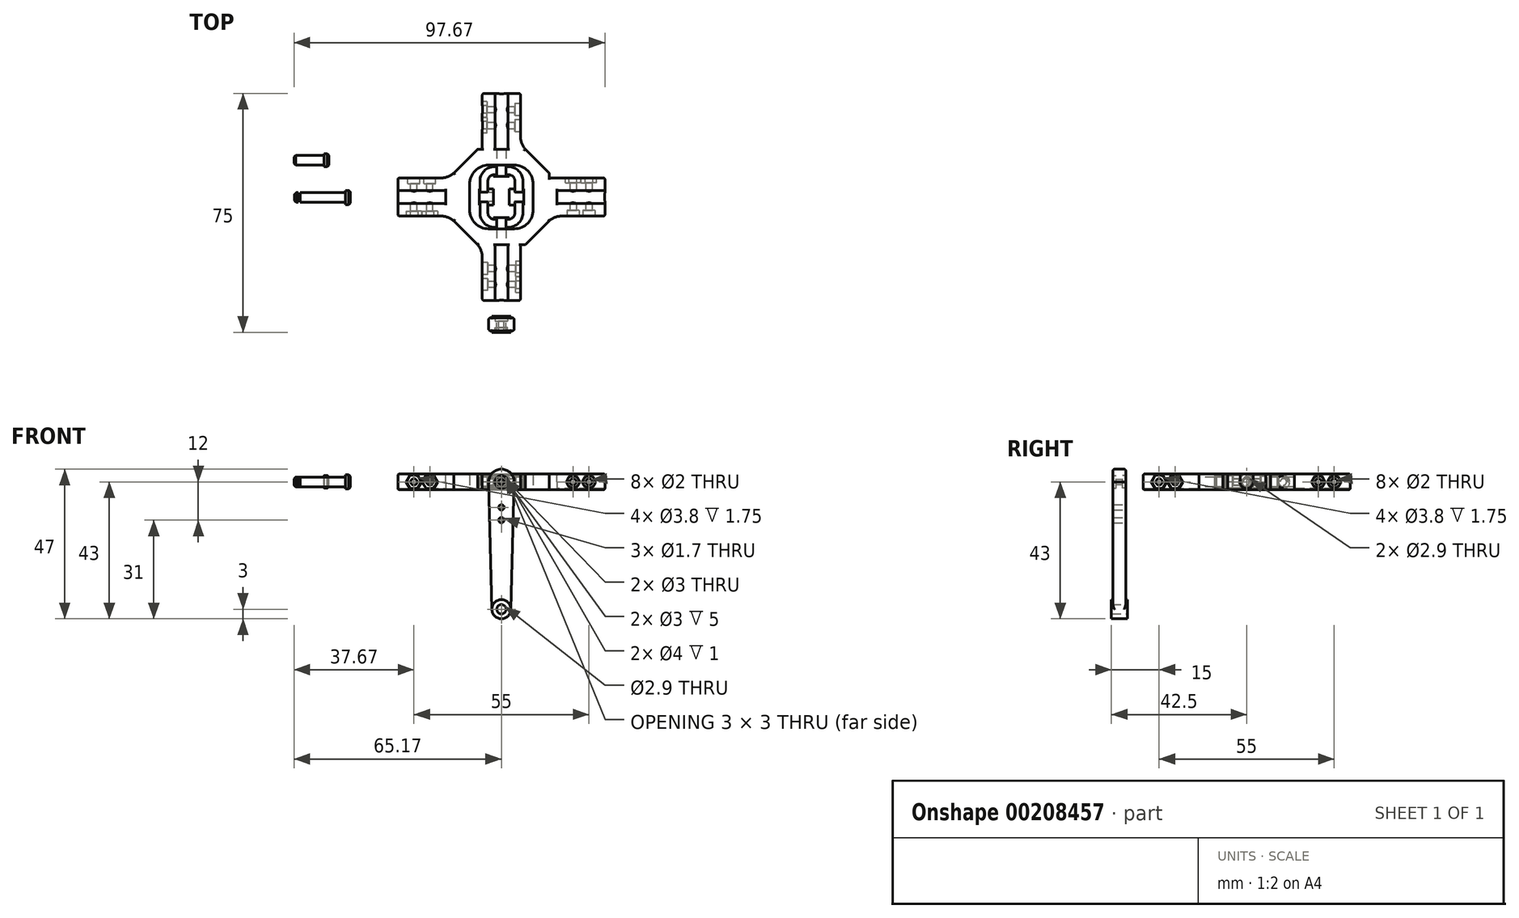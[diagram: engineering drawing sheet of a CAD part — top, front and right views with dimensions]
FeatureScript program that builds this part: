
annotation { "Feature Type Name" : "Feature", "Feature Type Description" : "" }
export const myFeature = defineFeature(function(context is Context, id is Id, definition is map)
    precondition{}
    {
        {
            var Q0;
            Q0=qCreatedBy(makeId("Front.planeOp"),FACE);
            var sketch = newSketch(context, id + "F0", { "sketchPlane" : qUnion([Q0])});
            skCircle(sketch, "E0", {"center": v(0, 0) * mm, "radius": 4 * mm});
            skCircle(sketch, "E1", {"center": v(0, -40) * mm, "radius": 3 * mm});
            skCircle(sketch, "E2", {"center": v(0, -40) * mm, "radius": 1.45 * mm});
            skLineSegment(sketch, "E3", {"start": v(-2, -37.76) * mm, "end": v(-2, -3.46) * mm});
            skLineSegment(sketch, "E4.MirrorCS", {"start": v(2, -37.76) * mm, "end": v(2, -3.46) * mm});
            skCircle(sketch, "E5", {"center": v(0, 0) * mm, "radius": 0.85 * mm});
            skCircle(sketch, "E6", {"center": v(0, -8) * mm, "radius": 0.85 * mm});
            skCircle(sketch, "E7", {"center": v(0, -12) * mm, "radius": 0.85 * mm});
            skCircle(sketch, "E8", {"center": v(0, 0) * mm, "radius": 2 * mm});
            skLineSegment(sketch, "E9", {"start": v(-4, 0) * mm, "end": v(-3, -40.07) * mm});
            skLineSegment(sketch, "E10", {"start": v(4, 0) * mm, "end": v(3, -40.07) * mm});
            skSolve(sketch);
        }
        {
            var Q0;
            {var subQ0=sQuery(id+"F0.wireOp",EDGE,"E0");var subQ1=makeQuery(id+"F0.imprint","INTERSECT",VERTEX,{"derivedFrom":[subQ0,sQuery(id+"F0.wireOp",EDGE,"E3")]});Q0=makeQuery(id+"F0.imprint","IMPRINT",FACE,{"disambiguationData":[TD([[makeQuery(id+"F0.imprint","IMPRINT",EDGE,{"disambiguationData":[TD([[subQ1,-1.0]])],"derivedFrom":subQ0}),1.0]])]});}
            var Q1;
            {var subQ0=sQuery(id+"F0.wireOp",EDGE,"E3");Q1=makeQuery(id+"F0.imprint","IMPRINT",FACE,{"disambiguationData":[TD([[makeQuery(id+"F0.imprint","IMPRINT",EDGE,{"derivedFrom":subQ0}),-1.0]])]});}
            var Q2;
            Q2=makeQuery(id+"F0.imprint","IMPRINT",FACE,{"disambiguationData":[TD([[makeQuery(id+"F0.imprint","IMPRINT",EDGE,{"derivedFrom":sQuery(id+"F0.wireOp",EDGE,"E5")}),-1.0]])]});
            var Q3;
            {var subQ0=sQuery(id+"F0.wireOp",EDGE,"E3");Q3=makeQuery(id+"F0.imprint","IMPRINT",FACE,{"disambiguationData":[TD([[makeQuery(id+"F0.imprint","IMPRINT",EDGE,{"derivedFrom":subQ0}),1.0]])]});}
            var Q4;
            {var subQ0=sQuery(id+"F0.wireOp",EDGE,"E4.MirrorCS");Q4=makeQuery(id+"F0.imprint","IMPRINT",FACE,{"disambiguationData":[TD([[makeQuery(id+"F0.imprint","IMPRINT",EDGE,{"derivedFrom":subQ0}),-1.0]])]});}
            extrude(context, id + "F1", {"entities" : qUnion([Q0, Q1, Q2, Q3, Q4]), "endBound" : BoundingType.SYMMETRIC, "depth" : 4 * mm});
        }
        {
            var Q0;
            Q0=makeQuery(id+"F0.imprint","IMPRINT",FACE,{"disambiguationData":[TD([[makeQuery(id+"F0.imprint","IMPRINT",EDGE,{"derivedFrom":sQuery(id+"F0.wireOp",EDGE,"E2")}),-1.0]])]});
            extrude(context, id + "F2", {"entities" : qUnion([Q0]), "operationType" : NewBodyOperationType.ADD, "endBound" : BoundingType.SYMMETRIC, "depth" : 5 * mm});
        }
        {
            var Q0;
            Q0=makeQuery(id+"F1.opExtrude","CAP_EDGE",EDGE,{"disambiguationData":[OSD([sQuery(id+"F0.wireOp",EDGE,"E9")])],"isStart":false});
            var Q1;
            Q1=makeQuery(id+"F1.opExtrude","CAP_EDGE",EDGE,{"disambiguationData":[OSD([sQuery(id+"F0.wireOp",EDGE,"E9")])],"isStart":true});
            var Q2;
            Q2=makeQuery(id+"F1.opExtrude","CAP_EDGE",EDGE,{"disambiguationData":[OSD([sQuery(id+"F0.wireOp",EDGE,"E10")])],"isStart":false});
            var Q3;
            Q3=makeQuery(id+"F1.opExtrude","CAP_EDGE",EDGE,{"disambiguationData":[OSD([sQuery(id+"F0.wireOp",EDGE,"E10")])],"isStart":true});
            var Q4;
            Q4=makeQuery(id+"F1.opExtrude","CAP_EDGE",EDGE,{"disambiguationData":[OSD([sQuery(id+"F0.wireOp",EDGE,"E0")])],"isStart":false});
            var Q5;
            Q5=makeQuery(id+"F1.opExtrude","CAP_EDGE",EDGE,{"disambiguationData":[OSD([sQuery(id+"F0.wireOp",EDGE,"E0")])],"isStart":true});
            fillet(context, id + "F3", {"entities" : qUnion([Q0, Q1, Q2, Q3, Q4, Q5]), "radius" : 0.5 * mm, "allowEdgeOverflow" : false});
        }
        {
            var Q0;
            Q0=makeQuery(id+"F0.imprint","IMPRINT",FACE,{"disambiguationData":[TD([[makeQuery(id+"F0.imprint","IMPRINT",EDGE,{"derivedFrom":sQuery(id+"F0.wireOp",EDGE,"E5")}),-1.0]])]});
            extrude(context, id + "F4", {"entities" : qUnion([Q0]), "operationType" : NewBodyOperationType.REMOVE, "depth" : 2 * mm, "hasSecondDirection" : true, "secondDirectionOppositeDirection" : false, "secondDirectionDepth" : 1 * mm});
        }
        {
            var Q0;
            Q0=makeQuery(id+"F0.imprint","IMPRINT",FACE,{"disambiguationData":[TD([[makeQuery(id+"F0.imprint","IMPRINT",EDGE,{"derivedFrom":sQuery(id+"F0.wireOp",EDGE,"E5")}),-1.0]])]});
            extrude(context, id + "F5", {"entities" : qUnion([Q0]), "operationType" : NewBodyOperationType.REMOVE, "oppositeDirection" : true, "depth" : 2 * mm, "hasSecondDirection" : true, "secondDirectionOppositeDirection" : true, "secondDirectionDepth" : 1 * mm});
        }
        {
            var Q0;
            Q0=qCreatedBy(makeId("Top.planeOp"),FACE);
            var sketch = newSketch(context, id + "F6", { "sketchPlane" : qUnion([Q0])});
            skLineSegment(sketch, "E11", {"start": v(7, 40) * mm, "end": v(-7, 40) * mm});
            skLineSegment(sketch, "E12", {"start": v(7, 40) * mm, "end": v(7, 42.5) * mm});
            skLineSegment(sketch, "E13", {"start": v(7, 42.5) * mm, "end": v(2.5, 42.5) * mm});
            skLineSegment(sketch, "E14", {"start": v(2.5, 42.5) * mm, "end": v(2.5, 40) * mm});
            skLineSegment(sketch, "E15.MirrorCS", {"start": v(-7, 40) * mm, "end": v(-7, 42.5) * mm});
            skLineSegment(sketch, "E16.MirrorCS", {"start": v(-7, 42.5) * mm, "end": v(-2.5, 42.5) * mm});
            skLineSegment(sketch, "E17.MirrorCS", {"start": v(-2.5, 42.5) * mm, "end": v(-2.5, 40) * mm});
            skLineSegment(sketch, "E18", {"start": v(0, 30) * mm, "end": v(0, 50) * mm});
            skLineSegment(sketch, "E19", {"start": v(0, 33.5) * mm, "end": v(-2.5, 33.5) * mm});
            skLineSegment(sketch, "E20", {"start": v(-2.5, 33.5) * mm, "end": v(-2.5, 30) * mm});
            skLineSegment(sketch, "E21.MirrorCS", {"start": v(0, 46.5) * mm, "end": v(-2.5, 46.5) * mm});
            skLineSegment(sketch, "E22.MirrorCS", {"start": v(-2.5, 46.5) * mm, "end": v(-2.5, 50) * mm});
            skLineSegment(sketch, "E23.bottom", {"start": v(-2.25, 49.5) * mm, "end": v(2.25, 49.5) * mm});
            skLineSegment(sketch, "E23.top", {"start": v(-2.25, 30.5) * mm, "end": v(2.25, 30.5) * mm});
            skLineSegment(sketch, "E23.left", {"start": v(-6.75, 45) * mm, "end": v(-6.75, 35) * mm});
            skLineSegment(sketch, "E23.right", {"start": v(6.75, 45) * mm, "end": v(6.75, 35) * mm});
            skLineSegment(sketch, "E24.bottom", {"start": v(-2.25, 47) * mm, "end": v(2.25, 47) * mm});
            skLineSegment(sketch, "E24.top", {"start": v(-2.25, 33) * mm, "end": v(2.25, 33) * mm});
            skLineSegment(sketch, "E24.left", {"start": v(-4.25, 45) * mm, "end": v(-4.25, 35) * mm});
            skLineSegment(sketch, "E24.right", {"start": v(4.25, 45) * mm, "end": v(4.25, 35) * mm});
            skLineSegment(sketch, "E25", {"start": v(-2.5, 30) * mm, "end": v(0, 30) * mm});
            skLineSegment(sketch, "E26.MirrorCS", {"start": v(-2.5, 50) * mm, "end": v(0, 50) * mm});
            skPoint(sketch, "E27.visualSharp", {"position": v(-4.25, 47) * mm});
            skArc(sketch, "E27.filletArc", {"start": v(-2.25, 47) * mm, "mid": v(-3.66, 46.41) * mm, "end": v(-4.25, 45) * mm});
            skPoint(sketch, "E28.visualSharp", {"position": v(4.25, 47) * mm});
            skArc(sketch, "E28.filletArc", {"start": v(4.25, 45) * mm, "mid": v(3.66, 46.41) * mm, "end": v(2.25, 47) * mm});
            skPoint(sketch, "E29.visualSharp", {"position": v(4.25, 33) * mm});
            skArc(sketch, "E29.filletArc", {"start": v(2.25, 33) * mm, "mid": v(3.66, 33.59) * mm, "end": v(4.25, 35) * mm});
            skPoint(sketch, "E30.visualSharp", {"position": v(-4.25, 33) * mm});
            skArc(sketch, "E30.filletArc", {"start": v(-4.25, 35) * mm, "mid": v(-3.66, 33.59) * mm, "end": v(-2.25, 33) * mm});
            skPoint(sketch, "E31.visualSharp", {"position": v(-6.75, 49.5) * mm});
            skArc(sketch, "E31.filletArc", {"start": v(-2.25, 49.5) * mm, "mid": v(-5.43, 48.18) * mm, "end": v(-6.75, 45) * mm});
            skPoint(sketch, "E32.visualSharp", {"position": v(6.75, 49.5) * mm});
            skArc(sketch, "E32.filletArc", {"start": v(6.75, 45) * mm, "mid": v(5.43, 48.18) * mm, "end": v(2.25, 49.5) * mm});
            skPoint(sketch, "E33.visualSharp", {"position": v(-6.75, 30.5) * mm});
            skArc(sketch, "E33.filletArc", {"start": v(-6.75, 35) * mm, "mid": v(-5.43, 31.82) * mm, "end": v(-2.25, 30.5) * mm});
            skPoint(sketch, "E34.visualSharp", {"position": v(6.75, 30.5) * mm});
            skArc(sketch, "E34.filletArc", {"start": v(2.25, 30.5) * mm, "mid": v(5.43, 31.82) * mm, "end": v(6.75, 35) * mm});
            skSolve(sketch);
        }
        {
            var Q0;
            {var subQ1=sQuery(id+"F6.wireOp",EDGE,"E23.left");var subQ3=sQuery(id+"F6.wireOp",EDGE,"E16.MirrorCS");var subQ4=makeQuery(id+"F6.imprint","INTERSECT",VERTEX,{"derivedFrom":[subQ3,subQ1]});Q0=makeQuery(id+"F6.imprint","IMPRINT",FACE,{"disambiguationData":[TD([[makeQuery(id+"F6.imprint","IMPRINT",EDGE,{"disambiguationData":[TD([[subQ4,-1.0]])],"derivedFrom":subQ3}),1.0]])]});}
            var Q1;
            {var subQ3=sQuery(id+"F6.wireOp",EDGE,"E18");var subQ8=sQuery(id+"F6.wireOp",EDGE,"E23.bottom");var subQ10=makeQuery(id+"F6.imprint","INTERSECT",VERTEX,{"derivedFrom":[subQ3,subQ8]});Q1=makeQuery(id+"F6.imprint","IMPRINT",FACE,{"disambiguationData":[TD([[makeQuery(id+"F6.imprint","IMPRINT",EDGE,{"disambiguationData":[TD([[subQ10,1.0]])],"derivedFrom":subQ3}),1.0]])]});}
            var Q2;
            {var subQ9=sQuery(id+"F6.wireOp",EDGE,"E28.filletArc");Q2=makeQuery(id+"F6.imprint","IMPRINT",FACE,{"disambiguationData":[TD([[makeQuery(id+"F6.imprint","IMPRINT",EDGE,{"derivedFrom":subQ9}),-1.0]])]});}
            var Q3;
            {var subQ0=sQuery(id+"F6.wireOp",EDGE,"E23.right");var subQ1=sQuery(id+"F6.wireOp",EDGE,"E11");var subQ2=makeQuery(id+"F6.imprint","INTERSECT",VERTEX,{"derivedFrom":[subQ1,subQ0]});Q3=makeQuery(id+"F6.imprint","IMPRINT",FACE,{"disambiguationData":[TD([[makeQuery(id+"F6.imprint","IMPRINT",EDGE,{"disambiguationData":[TD([[subQ2,-1.0]])],"derivedFrom":subQ1}),-1.0]])]});}
            var Q4;
            {var subQ7=sQuery(id+"F6.wireOp",EDGE,"E29.filletArc");Q4=makeQuery(id+"F6.imprint","IMPRINT",FACE,{"disambiguationData":[TD([[makeQuery(id+"F6.imprint","IMPRINT",EDGE,{"derivedFrom":subQ7}),-1.0]])]});}
            var Q5;
            {var subQ1=sQuery(id+"F6.wireOp",EDGE,"E23.top");var subQ3=sQuery(id+"F6.wireOp",EDGE,"E18");var subQ4=makeQuery(id+"F6.imprint","INTERSECT",VERTEX,{"derivedFrom":[subQ3,subQ1]});Q5=makeQuery(id+"F6.imprint","IMPRINT",FACE,{"disambiguationData":[TD([[makeQuery(id+"F6.imprint","IMPRINT",EDGE,{"disambiguationData":[TD([[subQ4,-1.0]])],"derivedFrom":subQ3}),1.0]])]});}
            var Q6;
            {var subQ1=sQuery(id+"F6.wireOp",EDGE,"E23.left");var subQ3=sQuery(id+"F6.wireOp",EDGE,"E11");var subQ4=makeQuery(id+"F6.imprint","INTERSECT",VERTEX,{"derivedFrom":[subQ3,subQ1]});Q6=makeQuery(id+"F6.imprint","IMPRINT",FACE,{"disambiguationData":[TD([[makeQuery(id+"F6.imprint","IMPRINT",EDGE,{"disambiguationData":[TD([[subQ4,1.0]])],"derivedFrom":subQ3}),1.0]])]});}
            var Q7;
            {var subQ0=sQuery(id+"F6.wireOp",EDGE,"E23.left");var subQ1=sQuery(id+"F6.wireOp",EDGE,"E11");var subQ2=makeQuery(id+"F6.imprint","INTERSECT",VERTEX,{"derivedFrom":[subQ1,subQ0]});Q7=makeQuery(id+"F6.imprint","IMPRINT",FACE,{"disambiguationData":[TD([[makeQuery(id+"F6.imprint","IMPRINT",EDGE,{"disambiguationData":[TD([[subQ2,1.0]])],"derivedFrom":subQ1}),-1.0]])]});}
            extrude(context, id + "F7", {"entities" : qUnion([Q0, Q1, Q2, Q3, Q4, Q5, Q6, Q7]), "endBound" : BoundingType.SYMMETRIC, "depth" : 4 * mm});
        }
        {
            var Q0;
            {var subQ0=sQuery(id+"F6.wireOp",EDGE,"E17.MirrorCS");Q0=makeQuery(id+"F6.imprint","IMPRINT",FACE,{"disambiguationData":[TD([[makeQuery(id+"F6.imprint","IMPRINT",EDGE,{"derivedFrom":subQ0}),-1.0]])]});}
            var Q1;
            {var subQ0=sQuery(id+"F6.wireOp",EDGE,"E15.MirrorCS");Q1=makeQuery(id+"F6.imprint","IMPRINT",FACE,{"disambiguationData":[TD([[makeQuery(id+"F6.imprint","IMPRINT",EDGE,{"derivedFrom":subQ0}),-1.0]])]});}
            var Q2;
            {var subQ0=sQuery(id+"F6.wireOp",EDGE,"E23.left");var subQ1=sQuery(id+"F6.wireOp",EDGE,"E11");var subQ2=makeQuery(id+"F6.imprint","INTERSECT",VERTEX,{"derivedFrom":[subQ1,subQ0]});Q2=makeQuery(id+"F6.imprint","IMPRINT",FACE,{"disambiguationData":[TD([[makeQuery(id+"F6.imprint","IMPRINT",EDGE,{"disambiguationData":[TD([[subQ2,1.0]])],"derivedFrom":subQ1}),-1.0]])]});}
            var Q3;
            {var subQ0=sQuery(id+"F6.wireOp",EDGE,"E14");Q3=makeQuery(id+"F6.imprint","IMPRINT",FACE,{"disambiguationData":[TD([[makeQuery(id+"F6.imprint","IMPRINT",EDGE,{"derivedFrom":subQ0}),1.0]])]});}
            var Q4;
            {var subQ0=sQuery(id+"F6.wireOp",EDGE,"E23.right");var subQ1=sQuery(id+"F6.wireOp",EDGE,"E11");var subQ2=makeQuery(id+"F6.imprint","INTERSECT",VERTEX,{"derivedFrom":[subQ1,subQ0]});Q4=makeQuery(id+"F6.imprint","IMPRINT",FACE,{"disambiguationData":[TD([[makeQuery(id+"F6.imprint","IMPRINT",EDGE,{"disambiguationData":[TD([[subQ2,-1.0]])],"derivedFrom":subQ1}),-1.0]])]});}
            var Q5;
            {var subQ0=sQuery(id+"F6.wireOp",EDGE,"E12");Q5=makeQuery(id+"F6.imprint","IMPRINT",FACE,{"disambiguationData":[TD([[makeQuery(id+"F6.imprint","IMPRINT",EDGE,{"derivedFrom":subQ0}),1.0]])]});}
            var Q6;
            Q6=sQuery(id+"F6.wireOp",EDGE,"E11");
            revolve(context, id + "F8", {"operationType" : NewBodyOperationType.ADD, "entities" : qUnion([Q0, Q1, Q2, Q3, Q4, Q5]), "axis" : qUnion([Q6]), "revolveType" : RevolveType.FULL});
        }
        {
            var Q0;
            {var subQ0=sQuery(id+"F6.wireOp",EDGE,"LlKhZmQs-V7VM-scmc-Wy5A-JgZZQCK02wPD");Q0=makeQuery(id+"F6.imprint","IMPRINT",FACE,{"disambiguationData":[TD([[makeQuery(id+"F6.imprint","IMPRINT",EDGE,{"derivedFrom":subQ0}),1.0]])]});}
            var Q1;
            {var subQ1=sQuery(id+"F6.wireOp",EDGE,"n0KZ0Nd7-8ER9-4vQ4-z3Lu-z5KG9LSxnQ1L");var subQ3=sQuery(id+"F6.wireOp",EDGE,"E20");var subQ4=makeQuery(id+"F6.imprint","INTERSECT",VERTEX,{"derivedFrom":[subQ1,subQ3]});Q1=makeQuery(id+"F6.imprint","IMPRINT",FACE,{"disambiguationData":[TD([[makeQuery(id+"F6.imprint","IMPRINT",EDGE,{"disambiguationData":[TD([[subQ4,-1.0]])],"derivedFrom":subQ1}),1.0]])]});}
            var Q2;
            {var subQ0=sQuery(id+"F6.wireOp",EDGE,"E19");Q2=makeQuery(id+"F6.imprint","IMPRINT",FACE,{"disambiguationData":[TD([[makeQuery(id+"F6.imprint","IMPRINT",EDGE,{"derivedFrom":subQ0}),1.0]])]});}
            var Q3;
            {var subQ0=sQuery(id+"F6.wireOp",EDGE,"E21.MirrorCS");Q3=makeQuery(id+"F6.imprint","IMPRINT",FACE,{"disambiguationData":[TD([[makeQuery(id+"F6.imprint","IMPRINT",EDGE,{"derivedFrom":subQ0}),-1.0]])]});}
            var Q4;
            {var subQ1=sQuery(id+"F6.wireOp",EDGE,"n0KZ0Nd7-8ER9-4vQ4-z3Lu-z5KG9LSxnQ1L");var subQ3=sQuery(id+"F6.wireOp",EDGE,"E22.MirrorCS");var subQ4=makeQuery(id+"F6.imprint","INTERSECT",VERTEX,{"derivedFrom":[subQ1,subQ3]});Q4=makeQuery(id+"F6.imprint","IMPRINT",FACE,{"disambiguationData":[TD([[makeQuery(id+"F6.imprint","IMPRINT",EDGE,{"disambiguationData":[TD([[subQ4,1.0]])],"derivedFrom":subQ1}),1.0]])]});}
            var Q5;
            {var subQ0=sQuery(id+"F6.wireOp",EDGE,"13f33fd6-691d-4f27-a9ab-e85cbf9f38f40.MirrorCS");Q5=makeQuery(id+"F6.imprint","IMPRINT",FACE,{"disambiguationData":[TD([[makeQuery(id+"F6.imprint","IMPRINT",EDGE,{"derivedFrom":subQ0}),-1.0]])]});}
            var Q6;
            {var subQ3=sQuery(id+"F6.wireOp",EDGE,"E18");var subQ8=sQuery(id+"F6.wireOp",EDGE,"E23.bottom");var subQ10=makeQuery(id+"F6.imprint","INTERSECT",VERTEX,{"derivedFrom":[subQ3,subQ8]});Q6=makeQuery(id+"F6.imprint","IMPRINT",FACE,{"disambiguationData":[TD([[makeQuery(id+"F6.imprint","IMPRINT",EDGE,{"disambiguationData":[TD([[subQ10,1.0]])],"derivedFrom":subQ3}),1.0]])]});}
            var Q7;
            {var subQ0=sQuery(id+"F6.wireOp",EDGE,"E26.MirrorCS");Q7=makeQuery(id+"F6.imprint","IMPRINT",FACE,{"disambiguationData":[TD([[makeQuery(id+"F6.imprint","IMPRINT",EDGE,{"derivedFrom":subQ0}),-1.0]])]});}
            var Q8;
            {var subQ1=sQuery(id+"F6.wireOp",EDGE,"E23.top");var subQ3=sQuery(id+"F6.wireOp",EDGE,"E18");var subQ4=makeQuery(id+"F6.imprint","INTERSECT",VERTEX,{"derivedFrom":[subQ3,subQ1]});Q8=makeQuery(id+"F6.imprint","IMPRINT",FACE,{"disambiguationData":[TD([[makeQuery(id+"F6.imprint","IMPRINT",EDGE,{"disambiguationData":[TD([[subQ4,-1.0]])],"derivedFrom":subQ3}),1.0]])]});}
            var Q9;
            {var subQ0=sQuery(id+"F6.wireOp",EDGE,"E25");Q9=makeQuery(id+"F6.imprint","IMPRINT",FACE,{"disambiguationData":[TD([[makeQuery(id+"F6.imprint","IMPRINT",EDGE,{"derivedFrom":subQ0}),1.0]])]});}
            var Q10;
            Q10=sQuery(id+"F6.wireOp",EDGE,"E18");
            revolve(context, id + "F9", {"operationType" : NewBodyOperationType.ADD, "entities" : qUnion([Q0, Q1, Q2, Q3, Q4, Q5, Q6, Q7, Q8, Q9]), "axis" : qUnion([Q10]), "revolveType" : RevolveType.FULL});
        }
        {
            var Q0;
            Q0=makeQuery(id+"F8.opRevolve","SWEPT_FACE",FACE,{"disambiguationData":[OSD([sQuery(id+"F6.wireOp",EDGE,"E15.MirrorCS")])]});
            var sketch = newSketch(context, id + "F10", { "sketchPlane" : qUnion([Q0])});
            skCircle(sketch, "E35", {"center": v(-40, 0) * mm, "radius": 1.45 * mm});
            skSolve(sketch);
        }
        {
            var Q0;
            Q0=makeQuery(id+"F10.imprint","IMPRINT",FACE,{"disambiguationData":[TD([[makeQuery(id+"F10.imprint","IMPRINT",EDGE,{"derivedFrom":sQuery(id+"F10.wireOp",EDGE,"E35")}),1.0]])]});
            extrude(context, id + "F11", {"entities" : qUnion([Q0]), "operationType" : NewBodyOperationType.REMOVE, "endBound" : BoundingType.THROUGH_ALL, "oppositeDirection" : true, "depth" : 25 * mm});
        }
        {
            var Q0;
            Q0=makeQuery(id+"F9.opRevolve","SWEPT_FACE",FACE,{"disambiguationData":[OSD([sQuery(id+"F6.wireOp",EDGE,"E25")])]});
            var sketch = newSketch(context, id + "F12", { "sketchPlane" : qUnion([Q0])});
            skCircle(sketch, "E36", {"center": v(0, 0) * mm, "radius": 1.5 * mm});
            skSolve(sketch);
        }
        {
            var Q0;
            Q0=makeQuery(id+"F12.imprint","IMPRINT",FACE,{"disambiguationData":[TD([[makeQuery(id+"F12.imprint","IMPRINT",EDGE,{"derivedFrom":sQuery(id+"F12.wireOp",EDGE,"E36")}),1.0]])]});
            extrude(context, id + "F13", {"entities" : qUnion([Q0]), "operationType" : NewBodyOperationType.REMOVE, "endBound" : BoundingType.THROUGH_ALL, "oppositeDirection" : true, "depth" : 25 * mm});
        }
        {
            var Q0;
            Q0=qCreatedBy(makeId("Top.planeOp"),FACE);
            var sketch = newSketch(context, id + "F14", { "sketchPlane" : qUnion([Q0])});
            skLineSegment(sketch, "E37.bottom", {"start": v(-10, 50) * mm, "end": v(10, 50) * mm});
            skLineSegment(sketch, "E37.top", {"start": v(-10, 30) * mm, "end": v(10, 30) * mm});
            skLineSegment(sketch, "E37.left", {"start": v(-10, 50) * mm, "end": v(-10, 30) * mm});
            skLineSegment(sketch, "E37.right", {"start": v(10, 50) * mm, "end": v(10, 30) * mm});
            skPoint(sketch, "E37.middle", {"position": v(0, 40) * mm});
            skCircle(sketch, "E38", {"center": v(0, 40) * mm, "radius": 10 * mm, "construction": true});
            skLineSegment(sketch, "E39.bottom", {"start": v(30, 10) * mm, "end": v(-30, 10) * mm});
            skLineSegment(sketch, "E39.top", {"start": v(30, 70) * mm, "end": v(-30, 70) * mm});
            skLineSegment(sketch, "E39.left", {"start": v(30, 10) * mm, "end": v(30, 70) * mm});
            skLineSegment(sketch, "E39.right", {"start": v(-30, 10) * mm, "end": v(-30, 70) * mm});
            skLineSegment(sketch, "E40", {"start": v(-7.5, 70) * mm, "end": v(-7.5, 55) * mm});
            skLineSegment(sketch, "E41", {"start": v(-7.5, 55) * mm, "end": v(-15, 47.5) * mm});
            skLineSegment(sketch, "E42", {"start": v(-15, 47.5) * mm, "end": v(-30, 47.5) * mm});
            skLineSegment(sketch, "E43", {"start": v(30, 70) * mm, "end": v(-30, 10) * mm, "construction": true});
            skLineSegment(sketch, "E44", {"start": v(-30, 40) * mm, "end": v(30, 40) * mm, "construction": true});
            skLineSegment(sketch, "E45.MirrorCS", {"start": v(30, 32.5) * mm, "end": v(15, 32.5) * mm});
            skLineSegment(sketch, "E46.MirrorCS", {"start": v(7.5, 25) * mm, "end": v(7.5, 10) * mm});
            skLineSegment(sketch, "E47.MirrorCS", {"start": v(15, 32.5) * mm, "end": v(7.5, 25) * mm});
            skLineSegment(sketch, "E48.MirrorCS", {"start": v(30, 47.5) * mm, "end": v(15, 47.5) * mm});
            skLineSegment(sketch, "E49.MirrorCS", {"start": v(15, 47.5) * mm, "end": v(7.5, 55) * mm});
            skLineSegment(sketch, "E50.MirrorCS", {"start": v(7.5, 55) * mm, "end": v(7.5, 70) * mm});
            skLineSegment(sketch, "E51.MirrorCS", {"start": v(-7.5, 10) * mm, "end": v(-7.5, 25) * mm});
            skLineSegment(sketch, "E52.MirrorCS", {"start": v(-7.5, 25) * mm, "end": v(-15, 32.5) * mm});
            skLineSegment(sketch, "E53.MirrorCS", {"start": v(-15, 32.5) * mm, "end": v(-30, 32.5) * mm});
            skLineSegment(sketch, "E54", {"start": v(-30, 42.05) * mm, "end": v(-15, 42.05) * mm});
            skLineSegment(sketch, "E55", {"start": v(-15, 42.05) * mm, "end": v(-15, 37.95) * mm});
            skLineSegment(sketch, "E56", {"start": v(-15, 37.95) * mm, "end": v(-30, 37.95) * mm});
            skLineSegment(sketch, "E57.MirrorCS", {"start": v(-2.05, 25) * mm, "end": v(-2.05, 10) * mm});
            skLineSegment(sketch, "E58.MirrorCS", {"start": v(2.05, 10) * mm, "end": v(2.05, 25) * mm});
            skLineSegment(sketch, "E59.MirrorCS", {"start": v(2.05, 25) * mm, "end": v(-2.05, 25) * mm});
            skLineSegment(sketch, "E60.MirrorCS", {"start": v(2.05, 70) * mm, "end": v(2.05, 55) * mm});
            skLineSegment(sketch, "E61.MirrorCS", {"start": v(2.05, 55) * mm, "end": v(-2.05, 55) * mm});
            skLineSegment(sketch, "E62.MirrorCS", {"start": v(-2.05, 55) * mm, "end": v(-2.05, 70) * mm});
            skLineSegment(sketch, "E63.MirrorCS", {"start": v(30, 42.05) * mm, "end": v(15, 42.05) * mm});
            skLineSegment(sketch, "E64.MirrorCS", {"start": v(15, 37.95) * mm, "end": v(30, 37.95) * mm});
            skLineSegment(sketch, "E65.MirrorCS", {"start": v(15, 42.05) * mm, "end": v(15, 37.95) * mm});
            skLineSegment(sketch, "E66", {"start": v(-7, 38.55) * mm, "end": v(-2.5, 38.55) * mm, "construction": true});
            skLineSegment(sketch, "E67", {"start": v(-2.5, 41.45) * mm, "end": v(-7, 41.45) * mm, "construction": true});
            skLineSegment(sketch, "E68", {"start": v(-15, 47.5) * mm, "end": v(-15, 32.5) * mm});
            skLineSegment(sketch, "E69", {"start": v(-7.5, 55) * mm, "end": v(7.5, 55) * mm});
            skLineSegment(sketch, "E70", {"start": v(15, 47.5) * mm, "end": v(15, 32.5) * mm});
            skLineSegment(sketch, "E71", {"start": v(7.5, 25) * mm, "end": v(-7.5, 25) * mm});
            skSolve(sketch);
        }
        {
            var Q0;
            {var subQ0=sQuery(id+"F14.wireOp",EDGE,"WiRYdTlx-Ytys-IKBb-qOmJ-XlPzdqFq3X80");var subQ1=sQuery(id+"F14.wireOp",EDGE,"hd7CA16K-ODOx-UwDL-788j-aqSsYlvFxQFE");var subQ2=makeQuery(id+"F14.imprint","INTERSECT",VERTEX,{"disambiguationData":[OD(1.0)],"derivedFrom":[subQ1,subQ0]});Q0=makeQuery(id+"F14.imprint","IMPRINT",FACE,{"disambiguationData":[TD([[makeQuery(id+"F14.imprint","IMPRINT",EDGE,{"disambiguationData":[TD([[subQ2,-1.0]])],"derivedFrom":subQ1}),-1.0]])]});}
            var Q1;
            {var subQ0=sQuery(id+"F14.wireOp",EDGE,"rD6La231-fMC7-wIai-GG1w-WcltRfGgBhv8");var subQ1=sQuery(id+"F14.wireOp",EDGE,"hd7CA16K-ODOx-UwDL-788j-aqSsYlvFxQFE");var subQ2=makeQuery(id+"F14.imprint","INTERSECT",VERTEX,{"derivedFrom":[subQ1,subQ0]});Q1=makeQuery(id+"F14.imprint","IMPRINT",FACE,{"disambiguationData":[TD([[makeQuery(id+"F14.imprint","IMPRINT",EDGE,{"disambiguationData":[TD([[subQ2,-1.0]])],"derivedFrom":subQ1}),-1.0]])]});}
            var Q2;
            {var subQ0=sQuery(id+"F14.wireOp",EDGE,"WiRYdTlx-Ytys-IKBb-qOmJ-XlPzdqFq3X80");var subQ1=sQuery(id+"F14.wireOp",EDGE,"hd7CA16K-ODOx-UwDL-788j-aqSsYlvFxQFE");var subQ2=makeQuery(id+"F14.imprint","INTERSECT",VERTEX,{"disambiguationData":[OD(0.0)],"derivedFrom":[subQ1,subQ0]});Q2=makeQuery(id+"F14.imprint","IMPRINT",FACE,{"disambiguationData":[TD([[makeQuery(id+"F14.imprint","IMPRINT",EDGE,{"disambiguationData":[TD([[subQ2,1.0]])],"derivedFrom":subQ1}),-1.0]])]});}
            var Q3;
            {var subQ0=sQuery(id+"F14.wireOp",EDGE,"7f476OY6-gB4X-IM5u-cAVR-7MiV8QXeFFAP");var subQ1=sQuery(id+"F14.wireOp",EDGE,"hd7CA16K-ODOx-UwDL-788j-aqSsYlvFxQFE");var subQ2=makeQuery(id+"F14.imprint","INTERSECT",VERTEX,{"disambiguationData":[OD(0.0)],"derivedFrom":[subQ1,subQ0]});Q3=makeQuery(id+"F14.imprint","IMPRINT",FACE,{"disambiguationData":[TD([[makeQuery(id+"F14.imprint","IMPRINT",EDGE,{"disambiguationData":[TD([[subQ2,1.0]])],"derivedFrom":subQ1}),-1.0]])]});}
            var Q4;
            {var subQ0=sQuery(id+"F14.wireOp",EDGE,"7f476OY6-gB4X-IM5u-cAVR-7MiV8QXeFFAP");var subQ1=sQuery(id+"F14.wireOp",EDGE,"hd7CA16K-ODOx-UwDL-788j-aqSsYlvFxQFE");var subQ2=makeQuery(id+"F14.imprint","INTERSECT",VERTEX,{"disambiguationData":[OD(0.0)],"derivedFrom":[subQ1,subQ0]});Q4=makeQuery(id+"F14.imprint","IMPRINT",FACE,{"disambiguationData":[TD([[makeQuery(id+"F14.imprint","IMPRINT",EDGE,{"disambiguationData":[TD([[subQ2,-1.0]])],"derivedFrom":subQ1}),-1.0]])]});}
            var Q5;
            {var subQ0=sQuery(id+"F14.wireOp",EDGE,"fcaab7d1-aade-45d0-acf4-e90b70e0a59d0.MirrorCS");var subQ1=sQuery(id+"F14.wireOp",EDGE,"hd7CA16K-ODOx-UwDL-788j-aqSsYlvFxQFE");var subQ2=makeQuery(id+"F14.imprint","INTERSECT",VERTEX,{"derivedFrom":[subQ1,subQ0]});Q5=makeQuery(id+"F14.imprint","IMPRINT",FACE,{"disambiguationData":[TD([[makeQuery(id+"F14.imprint","IMPRINT",EDGE,{"disambiguationData":[TD([[subQ2,-1.0]])],"derivedFrom":subQ1}),-1.0]])]});}
            var Q6;
            {var subQ0=sQuery(id+"F14.wireOp",EDGE,"bacef0e1-8516-4787-994b-6ca6d95049990.MirrorCS");Q6=makeQuery(id+"F14.imprint","IMPRINT",FACE,{"disambiguationData":[TD([[makeQuery(id+"F14.imprint","IMPRINT",EDGE,{"derivedFrom":subQ0}),-1.0]])]});}
            var Q7;
            {var subQ0=sQuery(id+"F14.wireOp",EDGE,"2fc310cb-db12-45d3-b044-d5ec6de6edb70.MirrorCS");Q7=makeQuery(id+"F14.imprint","IMPRINT",FACE,{"disambiguationData":[TD([[makeQuery(id+"F14.imprint","IMPRINT",EDGE,{"derivedFrom":subQ0}),-1.0]])]});}
            var Q8;
            {var subQ0=sQuery(id+"F14.wireOp",EDGE,"G2vHMd6c-AUWv-VVqk-8cvb-0UHsP2GUXyV1");Q8=makeQuery(id+"F14.imprint","IMPRINT",FACE,{"disambiguationData":[TD([[makeQuery(id+"F14.imprint","IMPRINT",EDGE,{"derivedFrom":subQ0}),1.0]])]});}
            var Q9;
            {var subQ0=sQuery(id+"F14.wireOp",EDGE,"fRm2VDpW-bxXU-Zf0j-BZ2m-yG7VDBASlDV1");Q9=makeQuery(id+"F14.imprint","IMPRINT",FACE,{"disambiguationData":[TD([[makeQuery(id+"F14.imprint","IMPRINT",EDGE,{"derivedFrom":subQ0}),1.0]])]});}
            var Q10;
            Q10=makeQuery(id+"F14.imprint","IMPRINT",FACE,{"disambiguationData":[TD([[makeQuery(id+"F14.imprint","IMPRINT",EDGE,{"derivedFrom":sQuery(id+"F14.wireOp",EDGE,"E37.bottom")}),1.0]])]});
            extrude(context, id + "F15", {"entities" : qUnion([Q0, Q1, Q2, Q3, Q4, Q5, Q6, Q7, Q8, Q9, Q10]), "endBound" : BoundingType.SYMMETRIC, "depth" : 5 * mm});
        }
        {
            var Q0;
            Q0=makeQuery(id+"F15.opExtrude","SWEPT_FACE",FACE,{"disambiguationData":[OSD([sQuery(id+"F14.wireOp",EDGE,"E71")])]});
            var sketch = newSketch(context, id + "F16", { "sketchPlane" : qUnion([Q0])});
            skCircle(sketch, "E72", {"center": v(0, 0) * mm, "radius": 1.5 * mm});
            skSolve(sketch);
        }
        {
            var Q0;
            Q0=makeQuery(id+"F16.imprint","IMPRINT",FACE,{"disambiguationData":[TD([[makeQuery(id+"F16.imprint","IMPRINT",EDGE,{"derivedFrom":sQuery(id+"F16.wireOp",EDGE,"E72")}),1.0]])]});
            extrude(context, id + "F17", {"entities" : qUnion([Q0]), "operationType" : NewBodyOperationType.REMOVE, "endBound" : BoundingType.THROUGH_ALL, "oppositeDirection" : true, "depth" : 25 * mm});
        }
        {
            var Q0;
            Q0=makeQuery(id+"F15.opExtrude","SWEPT_FACE",FACE,{"disambiguationData":[OSD([sQuery(id+"F14.wireOp",EDGE,"E71")])]});
            var sketch = newSketch(context, id + "F18", { "sketchPlane" : qUnion([Q0])});
            skCircle(sketch, "E73", {"center": v(0, 0) * mm, "radius": 2.05 * mm});
            skCircle(sketch, "E74", {"center": v(0, 0) * mm, "radius": 6 * mm});
            skLineSegment(sketch, "E75", {"start": v(-5.45, -2.5) * mm, "end": v(5.45, -2.5) * mm});
            skLineSegment(sketch, "E76", {"start": v(-5.45, 2.5) * mm, "end": v(5.45, 2.5) * mm});
            skLineSegment(sketch, "E77", {"start": v(-2.05, 0) * mm, "end": v(-2.05, 2.5) * mm});
            skLineSegment(sketch, "E78", {"start": v(2.05, 0) * mm, "end": v(2.05, 2.5) * mm});
            skLineSegment(sketch, "E79", {"start": v(6, 0) * mm, "end": v(6, 2.5) * mm});
            skLineSegment(sketch, "E80", {"start": v(6, 2.5) * mm, "end": v(5.45, 2.5) * mm});
            skLineSegment(sketch, "E81", {"start": v(-6, 0) * mm, "end": v(-6, 2.5) * mm});
            skLineSegment(sketch, "E82", {"start": v(-6, 2.5) * mm, "end": v(-5.45, 2.5) * mm});
            skLineSegment(sketch, "E83", {"start": v(6, 0) * mm, "end": v(6, -2.5) * mm});
            skLineSegment(sketch, "E84", {"start": v(6, -2.5) * mm, "end": v(5.45, -2.5) * mm});
            skLineSegment(sketch, "E85", {"start": v(-6, 0) * mm, "end": v(-6, -2.5) * mm});
            skLineSegment(sketch, "E86", {"start": v(-6, -2.5) * mm, "end": v(-5.45, -2.5) * mm});
            skSolve(sketch);
        }
        {
            var Q0;
            {var subQ0=sQuery(id+"F18.wireOp",EDGE,"E76");var subQ5=sQuery(id+"F18.wireOp",EDGE,"E77");var subQ7=makeQuery(id+"F18.imprint","INTERSECT",VERTEX,{"derivedFrom":[subQ0,subQ5]});Q0=makeQuery(id+"F18.imprint","IMPRINT",FACE,{"disambiguationData":[TD([[makeQuery(id+"F18.imprint","IMPRINT",EDGE,{"disambiguationData":[TD([[subQ7,1.0]])],"derivedFrom":subQ5}),1.0]])]});}
            var Q1;
            {var subQ0=sQuery(id+"F18.wireOp",EDGE,"E76");var subQ5=sQuery(id+"F18.wireOp",EDGE,"E78");var subQ6=makeQuery(id+"F18.imprint","INTERSECT",VERTEX,{"derivedFrom":[subQ0,subQ5]});Q1=makeQuery(id+"F18.imprint","IMPRINT",FACE,{"disambiguationData":[TD([[makeQuery(id+"F18.imprint","IMPRINT",EDGE,{"disambiguationData":[TD([[subQ6,1.0]])],"derivedFrom":subQ5}),-1.0]])]});}
            var Q2;
            {var subQ10=sQuery(id+"F18.wireOp",EDGE,"E77");var subQ11=sQuery(id+"F18.wireOp",EDGE,"E73");var subQ12=makeQuery(id+"F18.imprint","INTERSECT",VERTEX,{"derivedFrom":[subQ11,subQ10]});Q2=makeQuery(id+"F18.imprint","IMPRINT",FACE,{"disambiguationData":[TD([[makeQuery(id+"F18.imprint","IMPRINT",EDGE,{"disambiguationData":[TD([[subQ12,-1.0]])],"derivedFrom":subQ11}),-1.0]])]});}
            var Q3;
            {var subQ0=sQuery(id+"F18.wireOp",EDGE,"E76");var subQ5=sQuery(id+"F18.wireOp",EDGE,"E77");var subQ7=makeQuery(id+"F18.imprint","INTERSECT",VERTEX,{"derivedFrom":[subQ0,subQ5]});Q3=makeQuery(id+"F18.imprint","IMPRINT",FACE,{"disambiguationData":[TD([[makeQuery(id+"F18.imprint","IMPRINT",EDGE,{"disambiguationData":[TD([[subQ7,1.0]])],"derivedFrom":subQ5}),1.0]])]});}
            var Q4;
            {var subQ0=sQuery(id+"F18.wireOp",EDGE,"E80");Q4=makeQuery(id+"F18.imprint","IMPRINT",FACE,{"disambiguationData":[TD([[makeQuery(id+"F18.imprint","IMPRINT",EDGE,{"derivedFrom":subQ0}),1.0]])]});}
            var Q5;
            {var subQ0=sQuery(id+"F18.wireOp",EDGE,"E79");var subQ1=sQuery(id+"F18.wireOp",EDGE,"E74");var subQ2=makeQuery(id+"F18.imprint","INTERSECT",VERTEX,{"derivedFrom":[subQ1,subQ0]});Q5=makeQuery(id+"F18.imprint","IMPRINT",FACE,{"disambiguationData":[TD([[makeQuery(id+"F18.imprint","IMPRINT",EDGE,{"disambiguationData":[TD([[subQ2,-1.0]])],"derivedFrom":subQ1}),-1.0]])]});}
            var Q6;
            {var subQ0=sQuery(id+"F18.wireOp",EDGE,"E82");Q6=makeQuery(id+"F18.imprint","IMPRINT",FACE,{"disambiguationData":[TD([[makeQuery(id+"F18.imprint","IMPRINT",EDGE,{"derivedFrom":subQ0}),-1.0]])]});}
            var Q7;
            {var subQ0=sQuery(id+"F18.wireOp",EDGE,"E81");var subQ1=sQuery(id+"F18.wireOp",EDGE,"E74");var subQ2=makeQuery(id+"F18.imprint","INTERSECT",VERTEX,{"derivedFrom":[subQ1,subQ0]});Q7=makeQuery(id+"F18.imprint","IMPRINT",FACE,{"disambiguationData":[TD([[makeQuery(id+"F18.imprint","IMPRINT",EDGE,{"disambiguationData":[TD([[subQ2,1.0]])],"derivedFrom":subQ1}),-1.0]])]});}
            var Q8;
            {var subQ2=sQuery(id+"F18.wireOp",EDGE,"E83");Q8=makeQuery(id+"F18.imprint","IMPRINT",FACE,{"disambiguationData":[TD([[makeQuery(id+"F18.imprint","IMPRINT",EDGE,{"derivedFrom":subQ2}),-1.0]])]});}
            var Q9;
            {var subQ2=sQuery(id+"F18.wireOp",EDGE,"vOyl2B35-Enf8-pLNo-Xv3a-7ZgQyAOp5f5k");Q9=makeQuery(id+"F18.imprint","IMPRINT",FACE,{"disambiguationData":[TD([[makeQuery(id+"F18.imprint","IMPRINT",EDGE,{"derivedFrom":subQ2}),1.0]])]});}
            var Q10;
            {var subQ2=sQuery(id+"F18.wireOp",EDGE,"E85");Q10=makeQuery(id+"F18.imprint","IMPRINT",FACE,{"disambiguationData":[TD([[makeQuery(id+"F18.imprint","IMPRINT",EDGE,{"derivedFrom":subQ2}),1.0]])]});}
            extrude(context, id + "F19", {"entities" : qUnion([Q0, Q1, Q2, Q3, Q4, Q5, Q6, Q7, Q8, Q9, Q10]), "depth" : 17.5 * mm});
        }
        {
            var Q0;
            Q0=makeQuery(id+"F19.opExtrude","SWEPT_FACE",FACE,{"disambiguationData":[OSD([sQuery(id+"F18.wireOp",EDGE,"E81"),sQuery(id+"F18.wireOp",EDGE,"E85")])]});
            var sketch = newSketch(context, id + "F20", { "sketchPlane" : qUnion([Q0])});
            skCircle(sketch, "E87", {"center": v(-17.5, 0) * mm, "radius": 1 * mm});
            skCircle(sketch, "E88", {"center": v(-12.5, 0) * mm, "radius": 1 * mm});
            skCircle(sketch, "E89", {"center": v(-17.5, 0) * mm, "radius": 1.9 * mm});
            skCircle(sketch, "E90", {"center": v(-12.5, 0) * mm, "radius": 1.9 * mm});
            skSolve(sketch);
        }
        {
            var Q0;
            Q0=makeQuery(id+"F20.imprint","IMPRINT",FACE,{"disambiguationData":[TD([[makeQuery(id+"F20.imprint","IMPRINT",EDGE,{"derivedFrom":sQuery(id+"F20.wireOp",EDGE,"E87")}),1.0]])]});
            var Q1;
            Q1=makeQuery(id+"F20.imprint","IMPRINT",FACE,{"disambiguationData":[TD([[makeQuery(id+"F20.imprint","IMPRINT",EDGE,{"derivedFrom":sQuery(id+"F20.wireOp",EDGE,"E88")}),1.0]])]});
            extrude(context, id + "F21", {"entities" : qUnion([Q0, Q1]), "operationType" : NewBodyOperationType.REMOVE, "oppositeDirection" : true, "depth" : 25 * mm});
        }
        {
            var Q0;
            Q0=makeQuery(id+"F20.imprint","IMPRINT",FACE,{"disambiguationData":[TD([[makeQuery(id+"F20.imprint","IMPRINT",EDGE,{"derivedFrom":sQuery(id+"F20.wireOp",EDGE,"E87")}),-1.0]])]});
            var Q1;
            Q1=makeQuery(id+"F20.imprint","IMPRINT",FACE,{"disambiguationData":[TD([[makeQuery(id+"F20.imprint","IMPRINT",EDGE,{"derivedFrom":sQuery(id+"F20.wireOp",EDGE,"E88")}),-1.0]])]});
            extrude(context, id + "F22", {"entities" : qUnion([Q0, Q1]), "operationType" : NewBodyOperationType.REMOVE, "oppositeDirection" : true, "depth" : 1.75 * mm});
        }
        {
            var Q0;
            Q0=makeQuery(id+"F19.opExtrude","SWEPT_FACE",FACE,{"disambiguationData":[OSD([sQuery(id+"F18.wireOp",EDGE,"E79"),sQuery(id+"F18.wireOp",EDGE,"E83")])]});
            var sketch = newSketch(context, id + "F23", { "sketchPlane" : qUnion([Q0])});
            skCircle(sketch, "E91.cCircle", {"center": v(12.5, 0) * mm, "radius": 2.42 * mm, "construction": true});
            skLineSegment(sketch, "E91.0", {"start": v(13.71, -2.1) * mm, "end": v(11.29, -2.1) * mm});
            skLineSegment(sketch, "E91.1", {"start": v(11.29, -2.1) * mm, "end": v(10.08, 0) * mm});
            skLineSegment(sketch, "E91.2", {"start": v(10.08, 0) * mm, "end": v(11.29, 2.1) * mm});
            skLineSegment(sketch, "E91.3", {"start": v(11.29, 2.1) * mm, "end": v(13.71, 2.1) * mm});
            skLineSegment(sketch, "E91.4", {"start": v(13.71, 2.1) * mm, "end": v(14.92, 0) * mm});
            skLineSegment(sketch, "E91.5", {"start": v(14.92, 0) * mm, "end": v(13.71, -2.1) * mm});
            skCircle(sketch, "E92.cCircle", {"center": v(17.5, 0) * mm, "radius": 2.42 * mm, "construction": true});
            skLineSegment(sketch, "E92.0", {"start": v(18.71, -2.1) * mm, "end": v(16.29, -2.1) * mm});
            skLineSegment(sketch, "E92.1", {"start": v(16.29, -2.1) * mm, "end": v(15.08, 0) * mm});
            skLineSegment(sketch, "E92.2", {"start": v(15.08, 0) * mm, "end": v(16.29, 2.1) * mm});
            skLineSegment(sketch, "E92.3", {"start": v(16.29, 2.1) * mm, "end": v(18.71, 2.1) * mm});
            skLineSegment(sketch, "E92.4", {"start": v(18.71, 2.1) * mm, "end": v(19.92, 0) * mm});
            skLineSegment(sketch, "E92.5", {"start": v(19.92, 0) * mm, "end": v(18.71, -2.1) * mm});
            skSolve(sketch);
        }
        {
            var Q0;
            Q0=makeQuery(id+"F23.imprint","IMPRINT",FACE,{"disambiguationData":[TD([[makeQuery(id+"F23.imprint","IMPRINT",EDGE,{"derivedFrom":sQuery(id+"F23.wireOp",EDGE,"E91.0")}),-1.0]])]});
            var Q1;
            Q1=makeQuery(id+"F23.imprint","IMPRINT",FACE,{"disambiguationData":[TD([[makeQuery(id+"F23.imprint","IMPRINT",EDGE,{"derivedFrom":sQuery(id+"F23.wireOp",EDGE,"E92.0")}),-1.0]])]});
            extrude(context, id + "F24", {"entities" : qUnion([Q0, Q1]), "operationType" : NewBodyOperationType.REMOVE, "oppositeDirection" : true, "depth" : 1.5 * mm});
        }
        {
            var Q0;
            Q0=makeQuery(id+"F19.opExtrude","CAP_EDGE",EDGE,{"disambiguationData":[OSD([sQuery(id+"F18.wireOp",EDGE,"E81"),sQuery(id+"F18.wireOp",EDGE,"E85")])],"isStart":false});
            var Q1;
            Q1=makeQuery(id+"F19.opExtrude","CAP_EDGE",EDGE,{"disambiguationData":[OSD([sQuery(id+"F18.wireOp",EDGE,"E79"),sQuery(id+"F18.wireOp",EDGE,"E83")])],"isStart":false});
            var Q2;
            Q2=makeQuery(id+"F19.opExtrude","CAP_EDGE",EDGE,{"disambiguationData":[OSD([sQuery(id+"F18.wireOp",EDGE,"E75"),sQuery(id+"F18.wireOp",EDGE,"E84"),sQuery(id+"F18.wireOp",EDGE,"E86")])],"isStart":false});
            var Q3;
            Q3=makeQuery(id+"F19.opExtrude","CAP_EDGE",EDGE,{"disambiguationData":[OSD([sQuery(id+"F18.wireOp",EDGE,"E77")])],"isStart":false});
            fillet(context, id + "F25", {"entities" : qUnion([Q0, Q1, Q2, Q3]), "radius" : 0.5 * mm, "tangentPropagation" : true, "allowEdgeOverflow" : false});
        }
        {
            var Q0;
            Q0=qCreatedBy(makeId("Right.planeOp"),FACE);
            var sketch = newSketch(context, id + "F26", { "sketchPlane" : qUnion([Q0])});
            skLineSegment(sketch, "E93", {"start": v(40, -6.04) * mm, "end": v(40, 6.04) * mm, "construction": true});
            skCircle(sketch, "E94", {"center": v(40, 0) * mm, "radius": 3.36 * mm, "construction": true});
            skSolve(sketch);
        }
        {
            var Q0;
            Q0=makeQuery(id+"F19.opExtrude","SWEPT_BODY",BODY,{"disambiguationData":[OSD([sQuery(id+"F18.wireOp",EDGE,"E73"),sQuery(id+"F18.wireOp",EDGE,"E75"),sQuery(id+"F18.wireOp",EDGE,"E76"),sQuery(id+"F18.wireOp",EDGE,"E77"),sQuery(id+"F18.wireOp",EDGE,"E78"),sQuery(id+"F18.wireOp",EDGE,"E79"),sQuery(id+"F18.wireOp",EDGE,"E80"),sQuery(id+"F18.wireOp",EDGE,"E81"),sQuery(id+"F18.wireOp",EDGE,"E82"),sQuery(id+"F18.wireOp",EDGE,"E83"),sQuery(id+"F18.wireOp",EDGE,"E84"),sQuery(id+"F18.wireOp",EDGE,"vOyl2B35-Enf8-pLNo-Xv3a-7ZgQyAOp5f5k"),sQuery(id+"F18.wireOp",EDGE,"dBm5KtRB-nRU3-hO83-qJ6P-ldgX9l6JYJD6")])]});
            var Q1;
            Q1=sQuery(id+"F26.wireOp",EDGE,"E93");
            circularPattern(context, id + "F27", {"entities" : qUnion([Q0]), "axis" : qUnion([Q1]), "angle" : 360 * degree, "instanceCount" : 4, "equalSpace" : true});
        }
        {
            var Q0;
            Q0=makeQuery(id+"F15.opExtrude","SWEPT_BODY",BODY,{"disambiguationData":[OSD([sQuery(id+"F14.wireOp",EDGE,"E37.bottom"),sQuery(id+"F14.wireOp",EDGE,"E37.top"),sQuery(id+"F14.wireOp",EDGE,"E37.left"),sQuery(id+"F14.wireOp",EDGE,"E37.right"),sQuery(id+"F14.wireOp",EDGE,"E41"),sQuery(id+"F14.wireOp",EDGE,"E47.MirrorCS"),sQuery(id+"F14.wireOp",EDGE,"E49.MirrorCS"),sQuery(id+"F14.wireOp",EDGE,"E52.MirrorCS"),sQuery(id+"F14.wireOp",EDGE,"E68"),sQuery(id+"F14.wireOp",EDGE,"E69"),sQuery(id+"F14.wireOp",EDGE,"E70"),sQuery(id+"F14.wireOp",EDGE,"E71")])]});
            var Q1;
            Q1=makeQuery(id+"F19.opExtrude","SWEPT_BODY",BODY,{"disambiguationData":[OSD([sQuery(id+"F18.wireOp",EDGE,"E73"),sQuery(id+"F18.wireOp",EDGE,"E75"),sQuery(id+"F18.wireOp",EDGE,"E76"),sQuery(id+"F18.wireOp",EDGE,"E77"),sQuery(id+"F18.wireOp",EDGE,"E78"),sQuery(id+"F18.wireOp",EDGE,"E79"),sQuery(id+"F18.wireOp",EDGE,"E80"),sQuery(id+"F18.wireOp",EDGE,"E81"),sQuery(id+"F18.wireOp",EDGE,"E82"),sQuery(id+"F18.wireOp",EDGE,"E83"),sQuery(id+"F18.wireOp",EDGE,"E84"),sQuery(id+"F18.wireOp",EDGE,"vOyl2B35-Enf8-pLNo-Xv3a-7ZgQyAOp5f5k"),sQuery(id+"F18.wireOp",EDGE,"dBm5KtRB-nRU3-hO83-qJ6P-ldgX9l6JYJD6")])]});
            var Q2;
            Q2=makeQuery(id+"F27.opPattern","COPY",BODY,{"derivedFrom":makeQuery(id+"F19.opExtrude","SWEPT_BODY",BODY,{"disambiguationData":[OSD([sQuery(id+"F18.wireOp",EDGE,"E73"),sQuery(id+"F18.wireOp",EDGE,"E75"),sQuery(id+"F18.wireOp",EDGE,"E76"),sQuery(id+"F18.wireOp",EDGE,"E77"),sQuery(id+"F18.wireOp",EDGE,"E78"),sQuery(id+"F18.wireOp",EDGE,"E79"),sQuery(id+"F18.wireOp",EDGE,"E80"),sQuery(id+"F18.wireOp",EDGE,"E81"),sQuery(id+"F18.wireOp",EDGE,"E82"),sQuery(id+"F18.wireOp",EDGE,"E83"),sQuery(id+"F18.wireOp",EDGE,"E84"),sQuery(id+"F18.wireOp",EDGE,"vOyl2B35-Enf8-pLNo-Xv3a-7ZgQyAOp5f5k"),sQuery(id+"F18.wireOp",EDGE,"dBm5KtRB-nRU3-hO83-qJ6P-ldgX9l6JYJD6")])]}),"instanceName":"2"});
            var Q3;
            Q3=makeQuery(id+"F27.opPattern","COPY",BODY,{"derivedFrom":makeQuery(id+"F19.opExtrude","SWEPT_BODY",BODY,{"disambiguationData":[OSD([sQuery(id+"F18.wireOp",EDGE,"E73"),sQuery(id+"F18.wireOp",EDGE,"E75"),sQuery(id+"F18.wireOp",EDGE,"E76"),sQuery(id+"F18.wireOp",EDGE,"E77"),sQuery(id+"F18.wireOp",EDGE,"E78"),sQuery(id+"F18.wireOp",EDGE,"E79"),sQuery(id+"F18.wireOp",EDGE,"E80"),sQuery(id+"F18.wireOp",EDGE,"E81"),sQuery(id+"F18.wireOp",EDGE,"E82"),sQuery(id+"F18.wireOp",EDGE,"E83"),sQuery(id+"F18.wireOp",EDGE,"E84"),sQuery(id+"F18.wireOp",EDGE,"vOyl2B35-Enf8-pLNo-Xv3a-7ZgQyAOp5f5k"),sQuery(id+"F18.wireOp",EDGE,"dBm5KtRB-nRU3-hO83-qJ6P-ldgX9l6JYJD6")])]}),"instanceName":"1"});
            var Q4;
            Q4=makeQuery(id+"F27.opPattern","COPY",BODY,{"derivedFrom":makeQuery(id+"F19.opExtrude","SWEPT_BODY",BODY,{"disambiguationData":[OSD([sQuery(id+"F18.wireOp",EDGE,"E73"),sQuery(id+"F18.wireOp",EDGE,"E75"),sQuery(id+"F18.wireOp",EDGE,"E76"),sQuery(id+"F18.wireOp",EDGE,"E77"),sQuery(id+"F18.wireOp",EDGE,"E78"),sQuery(id+"F18.wireOp",EDGE,"E79"),sQuery(id+"F18.wireOp",EDGE,"E80"),sQuery(id+"F18.wireOp",EDGE,"E81"),sQuery(id+"F18.wireOp",EDGE,"E82"),sQuery(id+"F18.wireOp",EDGE,"E83"),sQuery(id+"F18.wireOp",EDGE,"E84"),sQuery(id+"F18.wireOp",EDGE,"vOyl2B35-Enf8-pLNo-Xv3a-7ZgQyAOp5f5k"),sQuery(id+"F18.wireOp",EDGE,"dBm5KtRB-nRU3-hO83-qJ6P-ldgX9l6JYJD6")])]}),"instanceName":"3"});
            booleanBodies(context, id + "F28", {"operationType" : BooleanOperationType.UNION, "tools" : qUnion([Q0, Q1, Q2, Q3, Q4])});
        }
        {
            var Q0;
            Q0=makeQuery(id+"F15.opExtrude","SWEPT_EDGE",EDGE,{"disambiguationData":[OSD([sQuery(id+"F14.wireOp",EDGE,"E37.bottom"),sQuery(id+"F14.wireOp",EDGE,"E37.left")])]});
            var Q1;
            Q1=makeQuery(id+"F15.opExtrude","SWEPT_EDGE",EDGE,{"disambiguationData":[OSD([sQuery(id+"F14.wireOp",EDGE,"E37.bottom"),sQuery(id+"F14.wireOp",EDGE,"E37.right")])]});
            var Q2;
            Q2=makeQuery(id+"F15.opExtrude","SWEPT_EDGE",EDGE,{"disambiguationData":[OSD([sQuery(id+"F14.wireOp",EDGE,"E37.top"),sQuery(id+"F14.wireOp",EDGE,"E37.left")])]});
            var Q3;
            Q3=makeQuery(id+"F15.opExtrude","SWEPT_EDGE",EDGE,{"disambiguationData":[OSD([sQuery(id+"F14.wireOp",EDGE,"E37.top"),sQuery(id+"F14.wireOp",EDGE,"E37.right")])]});
            var Q4;
            Q4=makeQuery(id+"F27.opPattern","COPY",EDGE,{"derivedFrom":makeQuery(id+"F19.opExtrude","CAP_EDGE",EDGE,{"disambiguationData":[OSD([sQuery(id+"F18.wireOp",EDGE,"E81"),sQuery(id+"F18.wireOp",EDGE,"vOyl2B35-Enf8-pLNo-Xv3a-7ZgQyAOp5f5k")])],"isStart":true}),"instanceName":"2"});
            var Q5;
            Q5=makeQuery(id+"F27.opPattern","COPY",EDGE,{"derivedFrom":makeQuery(id+"F19.opExtrude","CAP_EDGE",EDGE,{"disambiguationData":[OSD([sQuery(id+"F18.wireOp",EDGE,"E79"),sQuery(id+"F18.wireOp",EDGE,"E83")])],"isStart":true}),"instanceName":"1"});
            var Q6;
            Q6=makeQuery(id+"F27.opPattern","COPY",EDGE,{"derivedFrom":makeQuery(id+"F19.opExtrude","CAP_EDGE",EDGE,{"disambiguationData":[OSD([sQuery(id+"F18.wireOp",EDGE,"E79"),sQuery(id+"F18.wireOp",EDGE,"E83")])],"isStart":true}),"instanceName":"2"});
            var Q7;
            Q7=makeQuery(id+"F27.opPattern","COPY",EDGE,{"derivedFrom":makeQuery(id+"F19.opExtrude","CAP_EDGE",EDGE,{"disambiguationData":[OSD([sQuery(id+"F18.wireOp",EDGE,"E81"),sQuery(id+"F18.wireOp",EDGE,"vOyl2B35-Enf8-pLNo-Xv3a-7ZgQyAOp5f5k")])],"isStart":true}),"instanceName":"3"});
            var Q8;
            Q8=makeQuery(id+"F27.opPattern","COPY",EDGE,{"derivedFrom":makeQuery(id+"F19.opExtrude","CAP_EDGE",EDGE,{"disambiguationData":[OSD([sQuery(id+"F18.wireOp",EDGE,"E79"),sQuery(id+"F18.wireOp",EDGE,"E83")])],"isStart":true}),"instanceName":"3"});
            var Q9;
            Q9=makeQuery(id+"F19.opExtrude","CAP_EDGE",EDGE,{"disambiguationData":[OSD([sQuery(id+"F18.wireOp",EDGE,"E81"),sQuery(id+"F18.wireOp",EDGE,"vOyl2B35-Enf8-pLNo-Xv3a-7ZgQyAOp5f5k")])],"isStart":true});
            var Q10;
            Q10=makeQuery(id+"F19.opExtrude","CAP_EDGE",EDGE,{"disambiguationData":[OSD([sQuery(id+"F18.wireOp",EDGE,"E79"),sQuery(id+"F18.wireOp",EDGE,"E83")])],"isStart":true});
            var Q11;
            Q11=makeQuery(id+"F27.opPattern","COPY",EDGE,{"derivedFrom":makeQuery(id+"F19.opExtrude","CAP_EDGE",EDGE,{"disambiguationData":[OSD([sQuery(id+"F18.wireOp",EDGE,"E81"),sQuery(id+"F18.wireOp",EDGE,"vOyl2B35-Enf8-pLNo-Xv3a-7ZgQyAOp5f5k")])],"isStart":true}),"instanceName":"1"});
            fillet(context, id + "F29", {"entities" : qUnion([Q0, Q1, Q2, Q3, Q4, Q5, Q6, Q7, Q8, Q9, Q10, Q11]), "radius" : 6 * mm, "tangentPropagation" : true, "allowEdgeOverflow" : false});
        }
        {
            var Q0;
            {var subQ3=sQuery(id+"F14.wireOp",EDGE,"E68");Q0=makeQuery(id+"F28.opBoolean","SPLIT",FACE,{"disambiguationData":[TD([makeQuery(id+"F27.opPattern","COPY",FACE,{"derivedFrom":makeQuery(id+"F19.opExtrude","SWEPT_FACE",FACE,{"disambiguationData":[OSD([sQuery(id+"F18.wireOp",EDGE,"E73")])]}),"instanceName":"3"})])],"derivedFrom":makeQuery(id+"F15.opExtrude","SWEPT_FACE",FACE,{"disambiguationData":[OSD([subQ3])]})});}
            extrude(context, id + "F30", {"entities" : qUnion([Q0]), "operationType" : NewBodyOperationType.ADD, "depth" : 2.5 * mm});
        }
        {
            var Q0;
            {var subQ3=sQuery(id+"F14.wireOp",EDGE,"E70");Q0=makeQuery(id+"F28.opBoolean","SPLIT",FACE,{"disambiguationData":[TD([makeQuery(id+"F27.opPattern","COPY",FACE,{"derivedFrom":makeQuery(id+"F19.opExtrude","SWEPT_FACE",FACE,{"disambiguationData":[OSD([sQuery(id+"F18.wireOp",EDGE,"E73")])]}),"instanceName":"1"})])],"derivedFrom":makeQuery(id+"F15.opExtrude","SWEPT_FACE",FACE,{"disambiguationData":[OSD([subQ3])]})});}
            extrude(context, id + "F31", {"entities" : qUnion([Q0]), "operationType" : NewBodyOperationType.ADD, "depth" : 2.5 * mm});
        }
        {
            var Q0;
            Q0=makeQuery(id+"F15.opExtrude","CAP_EDGE",EDGE,{"disambiguationData":[OSD([sQuery(id+"F14.wireOp",EDGE,"E37.left")])],"isStart":false});
            var Q1;
            Q1=makeQuery(id+"F15.opExtrude","CAP_EDGE",EDGE,{"disambiguationData":[OSD([sQuery(id+"F14.wireOp",EDGE,"E52.MirrorCS")])],"isStart":false});
            var Q2;
            Q2=makeQuery(id+"F15.opExtrude","CAP_EDGE",EDGE,{"disambiguationData":[OSD([sQuery(id+"F14.wireOp",EDGE,"E52.MirrorCS")])],"isStart":true});
            var Q3;
            Q3=makeQuery(id+"F19.opExtrude","SWEPT_EDGE",EDGE,{"disambiguationData":[OSD([sQuery(id+"F14.wireOp",EDGE,"E71"),sQuery(id+"F18.wireOp",EDGE,"E81"),sQuery(id+"F18.wireOp",EDGE,"E82")])]});
            var Q4;
            Q4=makeQuery(id+"F19.opExtrude","SWEPT_EDGE",EDGE,{"disambiguationData":[OSD([sQuery(id+"F14.wireOp",EDGE,"E71"),sQuery(id+"F18.wireOp",EDGE,"E85"),sQuery(id+"F18.wireOp",EDGE,"E86")])]});
            var Q5;
            Q5=makeQuery(id+"F27.opPattern","COPY",EDGE,{"derivedFrom":makeQuery(id+"F19.opExtrude","SWEPT_EDGE",EDGE,{"disambiguationData":[OSD([sQuery(id+"F14.wireOp",EDGE,"E71"),sQuery(id+"F18.wireOp",EDGE,"E79"),sQuery(id+"F18.wireOp",EDGE,"E80")])]}),"instanceName":"3"});
            var Q6;
            Q6=makeQuery(id+"F27.opPattern","COPY",EDGE,{"derivedFrom":makeQuery(id+"F19.opExtrude","SWEPT_EDGE",EDGE,{"disambiguationData":[OSD([sQuery(id+"F14.wireOp",EDGE,"E71"),sQuery(id+"F18.wireOp",EDGE,"E81"),sQuery(id+"F18.wireOp",EDGE,"E82")])]}),"instanceName":"3"});
            var Q7;
            Q7=makeQuery(id+"F15.opExtrude","CAP_EDGE",EDGE,{"disambiguationData":[OSD([sQuery(id+"F14.wireOp",EDGE,"E41")])],"isStart":false});
            var Q8;
            Q8=makeQuery(id+"F15.opExtrude","CAP_EDGE",EDGE,{"disambiguationData":[OSD([sQuery(id+"F14.wireOp",EDGE,"E47.MirrorCS")])],"isStart":false});
            var Q9;
            Q9=makeQuery(id+"F15.opExtrude","CAP_EDGE",EDGE,{"disambiguationData":[OSD([sQuery(id+"F14.wireOp",EDGE,"E49.MirrorCS")])],"isStart":false});
            var Q10;
            Q10=makeQuery(id+"F27.opPattern","COPY",EDGE,{"derivedFrom":makeQuery(id+"F19.opExtrude","SWEPT_EDGE",EDGE,{"disambiguationData":[OSD([sQuery(id+"F14.wireOp",EDGE,"E71"),sQuery(id+"F18.wireOp",EDGE,"E81"),sQuery(id+"F18.wireOp",EDGE,"E82")])]}),"instanceName":"2"});
            var Q11;
            Q11=makeQuery(id+"F27.opPattern","COPY",EDGE,{"derivedFrom":makeQuery(id+"F19.opExtrude","SWEPT_EDGE",EDGE,{"disambiguationData":[OSD([sQuery(id+"F14.wireOp",EDGE,"E71"),sQuery(id+"F18.wireOp",EDGE,"E79"),sQuery(id+"F18.wireOp",EDGE,"E80")])]}),"instanceName":"1"});
            var Q12;
            Q12=makeQuery(id+"F27.opPattern","COPY",EDGE,{"derivedFrom":makeQuery(id+"F19.opExtrude","SWEPT_EDGE",EDGE,{"disambiguationData":[OSD([sQuery(id+"F14.wireOp",EDGE,"E71"),sQuery(id+"F18.wireOp",EDGE,"E79"),sQuery(id+"F18.wireOp",EDGE,"E80")])]}),"instanceName":"2"});
            var Q13;
            Q13=makeQuery(id+"F19.opExtrude","SWEPT_EDGE",EDGE,{"disambiguationData":[OSD([sQuery(id+"F14.wireOp",EDGE,"E71"),sQuery(id+"F18.wireOp",EDGE,"E79"),sQuery(id+"F18.wireOp",EDGE,"E80")])]});
            var Q14;
            Q14=makeQuery(id+"F27.opPattern","COPY",EDGE,{"derivedFrom":makeQuery(id+"F19.opExtrude","SWEPT_EDGE",EDGE,{"disambiguationData":[OSD([sQuery(id+"F14.wireOp",EDGE,"E71"),sQuery(id+"F18.wireOp",EDGE,"E81"),sQuery(id+"F18.wireOp",EDGE,"E82")])]}),"instanceName":"1"});
            var Q15;
            Q15=makeQuery(id+"F15.opExtrude","CAP_EDGE",EDGE,{"disambiguationData":[OSD([sQuery(id+"F14.wireOp",EDGE,"E47.MirrorCS")])],"isStart":true});
            var Q16;
            Q16=makeQuery(id+"F15.opExtrude","CAP_EDGE",EDGE,{"disambiguationData":[OSD([sQuery(id+"F14.wireOp",EDGE,"E49.MirrorCS")])],"isStart":true});
            var Q17;
            Q17=makeQuery(id+"F15.opExtrude","CAP_EDGE",EDGE,{"disambiguationData":[OSD([sQuery(id+"F14.wireOp",EDGE,"E41")])],"isStart":true});
            var Q18;
            Q18=makeQuery(id+"F19.opExtrude","SWEPT_EDGE",EDGE,{"disambiguationData":[OSD([sQuery(id+"F14.wireOp",EDGE,"E71"),sQuery(id+"F18.wireOp",EDGE,"E83"),sQuery(id+"F18.wireOp",EDGE,"E84")])]});
            var Q19;
            Q19=makeQuery(id+"F27.opPattern","COPY",EDGE,{"derivedFrom":makeQuery(id+"F19.opExtrude","SWEPT_EDGE",EDGE,{"disambiguationData":[OSD([sQuery(id+"F14.wireOp",EDGE,"E71"),sQuery(id+"F18.wireOp",EDGE,"E85"),sQuery(id+"F18.wireOp",EDGE,"E86")])]}),"instanceName":"1"});
            var Q20;
            Q20=makeQuery(id+"F27.opPattern","COPY",EDGE,{"derivedFrom":makeQuery(id+"F19.opExtrude","SWEPT_EDGE",EDGE,{"disambiguationData":[OSD([sQuery(id+"F14.wireOp",EDGE,"E71"),sQuery(id+"F18.wireOp",EDGE,"E83"),sQuery(id+"F18.wireOp",EDGE,"E84")])]}),"instanceName":"1"});
            var Q21;
            Q21=makeQuery(id+"F27.opPattern","COPY",EDGE,{"derivedFrom":makeQuery(id+"F19.opExtrude","SWEPT_EDGE",EDGE,{"disambiguationData":[OSD([sQuery(id+"F14.wireOp",EDGE,"E71"),sQuery(id+"F18.wireOp",EDGE,"E83"),sQuery(id+"F18.wireOp",EDGE,"E84")])]}),"instanceName":"3"});
            var Q22;
            Q22=makeQuery(id+"F27.opPattern","COPY",EDGE,{"derivedFrom":makeQuery(id+"F19.opExtrude","SWEPT_EDGE",EDGE,{"disambiguationData":[OSD([sQuery(id+"F14.wireOp",EDGE,"E71"),sQuery(id+"F18.wireOp",EDGE,"E85"),sQuery(id+"F18.wireOp",EDGE,"E86")])]}),"instanceName":"3"});
            var Q23;
            Q23=makeQuery(id+"F27.opPattern","COPY",EDGE,{"derivedFrom":makeQuery(id+"F19.opExtrude","SWEPT_EDGE",EDGE,{"disambiguationData":[OSD([sQuery(id+"F14.wireOp",EDGE,"E71"),sQuery(id+"F18.wireOp",EDGE,"E85"),sQuery(id+"F18.wireOp",EDGE,"E86")])]}),"instanceName":"2"});
            var Q24;
            Q24=makeQuery(id+"F27.opPattern","COPY",EDGE,{"derivedFrom":makeQuery(id+"F19.opExtrude","SWEPT_EDGE",EDGE,{"disambiguationData":[OSD([sQuery(id+"F14.wireOp",EDGE,"E71"),sQuery(id+"F18.wireOp",EDGE,"E83"),sQuery(id+"F18.wireOp",EDGE,"E84")])]}),"instanceName":"2"});
            fillet(context, id + "F32", {"entities" : qUnion([Q0, Q1, Q2, Q3, Q4, Q5, Q6, Q7, Q8, Q9, Q10, Q11, Q12, Q13, Q14, Q15, Q16, Q17, Q18, Q19, Q20, Q21, Q22, Q23, Q24]), "radius" : 0.5 * mm, "tangentPropagation" : true, "allowEdgeOverflow" : false});
        }
        {
            var Q0;
            Q0=qCreatedBy(makeId("Top.planeOp"),FACE);
            var sketch = newSketch(context, id + "F33", { "sketchPlane" : qUnion([Q0])});
            skLineSegment(sketch, "E95", {"start": v(-64.97, 40.84) * mm, "end": v(-64.47, 41.34) * mm});
            skLineSegment(sketch, "E96", {"start": v(-64.47, 41.34) * mm, "end": v(-48.97, 41.34) * mm});
            skLineSegment(sketch, "E97", {"start": v(-48.97, 41.34) * mm, "end": v(-48.97, 42.1) * mm});
            skLineSegment(sketch, "E98", {"start": v(-48.97, 42.1) * mm, "end": v(-47.97, 42.1) * mm});
            skLineSegment(sketch, "E99", {"start": v(-47.97, 42.1) * mm, "end": v(-47.47, 41.6) * mm});
            skLineSegment(sketch, "E100", {"start": v(-47.47, 41.6) * mm, "end": v(-47.47, 39.84) * mm});
            skLineSegment(sketch, "E101", {"start": v(-47.47, 39.84) * mm, "end": v(-64.97, 39.84) * mm});
            skLineSegment(sketch, "E102", {"start": v(-64.97, 39.84) * mm, "end": v(-64.97, 40.84) * mm});
            skLineSegment(sketch, "E103", {"start": v(-63.87, 41.34) * mm, "end": v(-63.87, 40.78) * mm});
            skLineSegment(sketch, "E104", {"start": v(-63.87, 40.78) * mm, "end": v(-63.17, 40.78) * mm});
            skLineSegment(sketch, "E105", {"start": v(-63.17, 40.78) * mm, "end": v(-63.17, 41.34) * mm});
            skSolve(sketch);
        }
        {
            var Q0;
            Q0=makeQuery(id+"F33.imprint","IMPRINT",FACE,{"disambiguationData":[TD([[makeQuery(id+"F33.imprint","IMPRINT",EDGE,{"derivedFrom":sQuery(id+"F33.wireOp",EDGE,"E95")}),-1.0]])]});
            var Q1;
            Q1=sQuery(id+"F33.wireOp",EDGE,"E101");
            revolve(context, id + "F34", {"entities" : qUnion([Q0]), "axis" : qUnion([Q1]), "revolveType" : RevolveType.FULL});
        }
        {
            var Q0;
            Q0=qCreatedBy(makeId("Top.planeOp"),FACE);
            var sketch = newSketch(context, id + "F35", { "sketchPlane" : qUnion([Q0])});
            skLineSegment(sketch, "E106", {"start": v(-65.17, 52.54) * mm, "end": v(-64.67, 53.04) * mm});
            skLineSegment(sketch, "E107", {"start": v(-64.67, 53.04) * mm, "end": v(-55.67, 53.04) * mm});
            skLineSegment(sketch, "E108", {"start": v(-55.67, 53.04) * mm, "end": v(-55.67, 53.54) * mm});
            skLineSegment(sketch, "E109", {"start": v(-55.67, 53.54) * mm, "end": v(-54.67, 53.54) * mm});
            skLineSegment(sketch, "E110", {"start": v(-54.67, 53.54) * mm, "end": v(-54.17, 53.04) * mm});
            skLineSegment(sketch, "E111", {"start": v(-54.17, 53.04) * mm, "end": v(-54.17, 51.54) * mm});
            skLineSegment(sketch, "E112", {"start": v(-54.17, 51.54) * mm, "end": v(-65.17, 51.54) * mm});
            skLineSegment(sketch, "E113", {"start": v(-65.17, 51.54) * mm, "end": v(-65.17, 52.54) * mm});
            skSolve(sketch);
        }
        {
            var Q0;
            Q0=makeQuery(id+"F35.imprint","IMPRINT",FACE,{"disambiguationData":[TD([[makeQuery(id+"F35.imprint","IMPRINT",EDGE,{"derivedFrom":sQuery(id+"F35.wireOp",EDGE,"E106")}),-1.0]])]});
            var Q1;
            Q1=sQuery(id+"F35.wireOp",EDGE,"E112");
            revolve(context, id + "F36", {"entities" : qUnion([Q0]), "axis" : qUnion([Q1]), "revolveType" : RevolveType.FULL});
        }
    });
